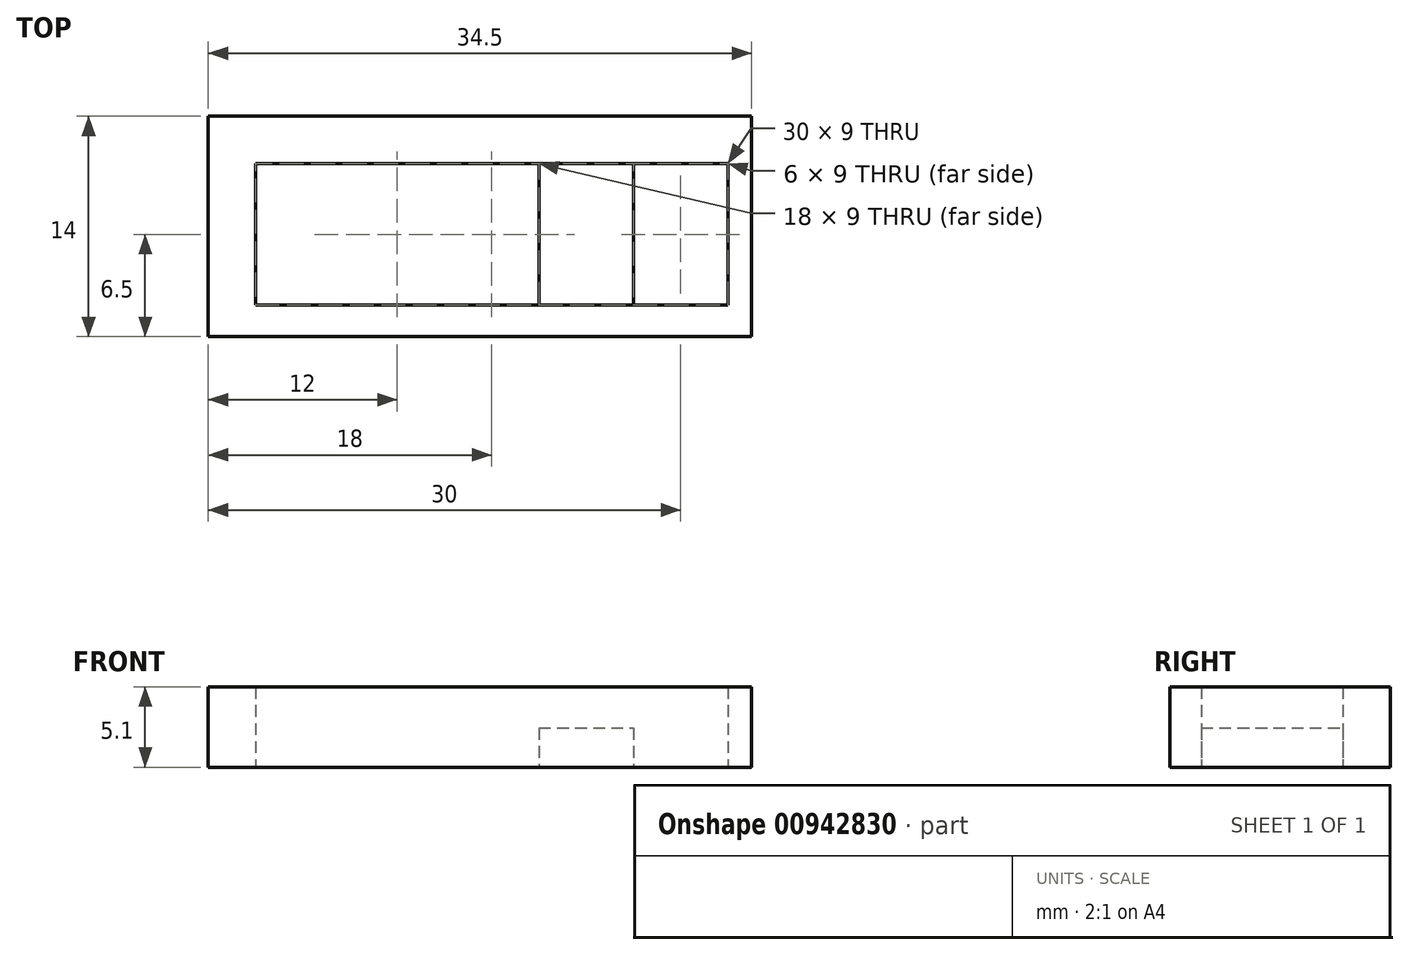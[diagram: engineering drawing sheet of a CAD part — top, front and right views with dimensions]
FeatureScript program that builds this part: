
annotation { "Feature Type Name" : "Feature", "Feature Type Description" : "" }
export const myFeature = defineFeature(function(context is Context, id is Id, definition is map)
    precondition{}
    {
        {
            var Q0;
            Q0=qCreatedBy(makeId("Top.planeOp"),FACE);
            var sketch = newSketch(context, id + "F0", { "sketchPlane" : qUnion([Q0])});
            skLineSegment(sketch, "E0.bottom", {"start": v(0, 0) * mm, "end": v(34.5, 0) * mm});
            skLineSegment(sketch, "E0.top", {"start": v(0, 14) * mm, "end": v(34.5, 14) * mm});
            skLineSegment(sketch, "E0.left", {"start": v(0, 0) * mm, "end": v(0, 14) * mm});
            skLineSegment(sketch, "E0.right", {"start": v(34.5, 0) * mm, "end": v(34.5, 14) * mm});
            skLineSegment(sketch, "E1.bottom", {"start": v(3, 2) * mm, "end": v(21, 2) * mm});
            skLineSegment(sketch, "E1.top", {"start": v(3, 11) * mm, "end": v(21, 11) * mm});
            skLineSegment(sketch, "E1.left", {"start": v(3, 2) * mm, "end": v(3, 11) * mm});
            skLineSegment(sketch, "E1.right", {"start": v(21, 2) * mm, "end": v(21, 11) * mm});
            skLineSegment(sketch, "E2.bottom", {"start": v(27, 2) * mm, "end": v(33, 2) * mm});
            skLineSegment(sketch, "E2.top", {"start": v(27, 11) * mm, "end": v(33, 11) * mm});
            skLineSegment(sketch, "E2.left", {"start": v(33, 2) * mm, "end": v(33, 11) * mm});
            skLineSegment(sketch, "E2.right", {"start": v(27, 2) * mm, "end": v(27, 11) * mm});
            skSolve(sketch);
        }
        {
            var Q0;
            Q0=makeQuery(id+"F0.imprint","IMPRINT",FACE,{"disambiguationData":[TD([[makeQuery(id+"F0.imprint","IMPRINT",EDGE,{"derivedFrom":sQuery(id+"F0.wireOp",EDGE,"E0.bottom")}),1.0]])]});
            extrude(context, id + "F1", {"entities" : qUnion([Q0]), "depth" : 5.1 * mm, "offsetDistance" : 25 * mm});
        }
        {
            var Q0;
            Q0=makeQuery(id+"F1.opExtrude","CAP_FACE",FACE,{"disambiguationData":[OSD([sQuery(id+"F0.wireOp",EDGE,"E0.bottom"),sQuery(id+"F0.wireOp",EDGE,"E0.top"),sQuery(id+"F0.wireOp",EDGE,"E0.left"),sQuery(id+"F0.wireOp",EDGE,"E0.right"),sQuery(id+"F0.wireOp",EDGE,"E1.bottom"),sQuery(id+"F0.wireOp",EDGE,"E1.top"),sQuery(id+"F0.wireOp",EDGE,"E1.left"),sQuery(id+"F0.wireOp",EDGE,"E1.right"),sQuery(id+"F0.wireOp",EDGE,"E2.bottom"),sQuery(id+"F0.wireOp",EDGE,"E2.top"),sQuery(id+"F0.wireOp",EDGE,"E2.left"),sQuery(id+"F0.wireOp",EDGE,"E2.right")])],"isStart":false});
            var sketch = newSketch(context, id + "F2", { "sketchPlane" : qUnion([Q0])});
            skLineSegment(sketch, "E3.bottom", {"start": v(21, 11) * mm, "end": v(27.85, 11) * mm});
            skLineSegment(sketch, "E3.top", {"start": v(21, 2) * mm, "end": v(27.85, 2) * mm});
            skLineSegment(sketch, "E3.left", {"start": v(21, 11) * mm, "end": v(21, 2) * mm});
            skLineSegment(sketch, "E3.right", {"start": v(27.85, 11) * mm, "end": v(27.85, 2) * mm});
            skSolve(sketch);
        }
        {
            var Q0;
            {var subQ0=sQuery(id+"F2.wireOp",EDGE,"E3.left");Q0=makeQuery(id+"F2.imprint","IMPRINT",FACE,{"disambiguationData":[TD([[makeQuery(id+"F2.imprint","IMPRINT",EDGE,{"derivedFrom":subQ0}),-1.0]])]});}
            extrude(context, id + "F3", {"entities" : qUnion([Q0]), "operationType" : NewBodyOperationType.REMOVE, "oppositeDirection" : true, "depth" : 5.1 * mm - 2.5 * mm, "offsetDistance" : 25 * mm});
        }
    });
